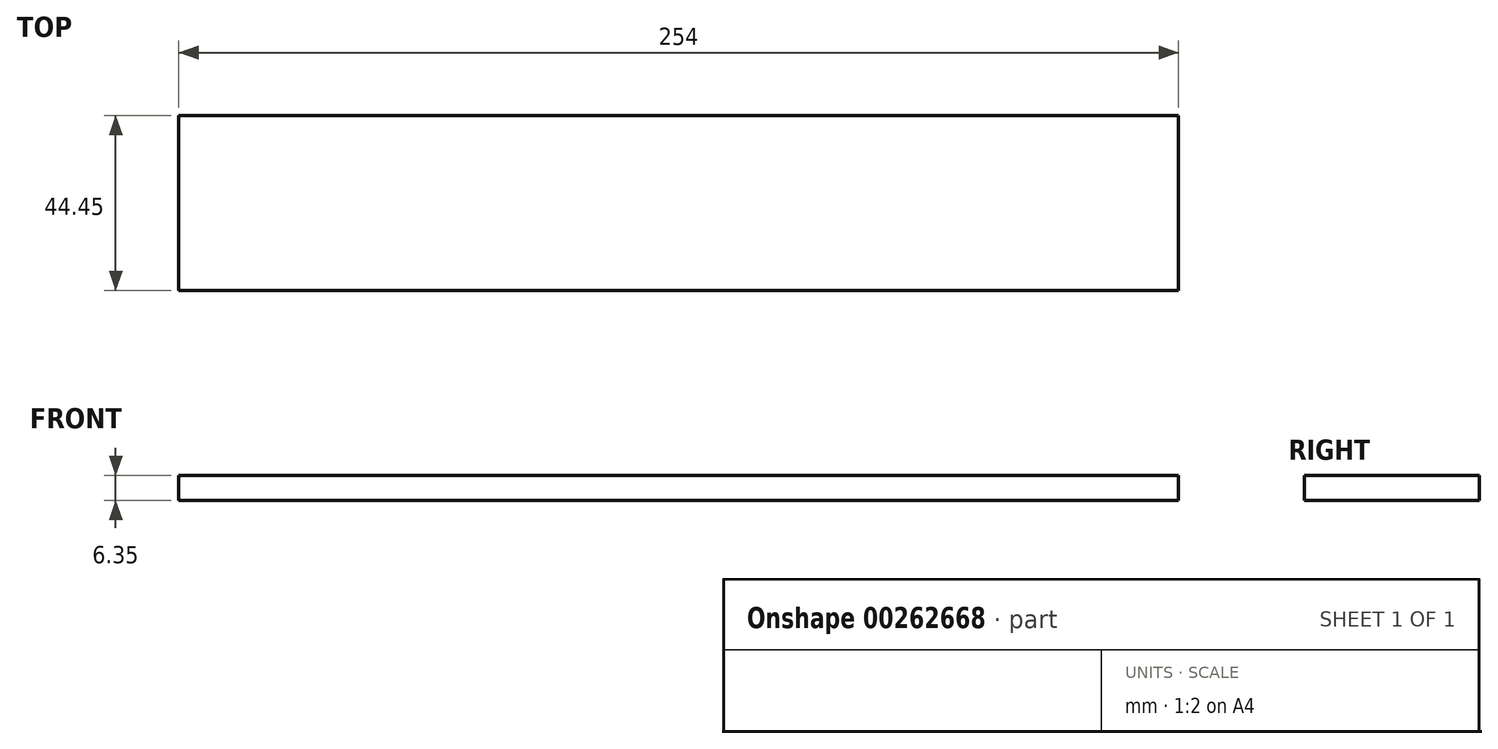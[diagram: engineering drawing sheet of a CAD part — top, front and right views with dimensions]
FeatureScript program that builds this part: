
annotation { "Feature Type Name" : "Feature", "Feature Type Description" : "" }
export const myFeature = defineFeature(function(context is Context, id is Id, definition is map)
    precondition{}
    {
        {
            var Q0;
            Q0=qCreatedBy(makeId("Top.planeOp"),FACE);
            var sketch = newSketch(context, id + "F0", { "sketchPlane" : qUnion([Q0])});
            skLineSegment(sketch, "E0.bottom", {"start": v(0, 0) * mm, "end": v(254, 0) * mm});
            skLineSegment(sketch, "E0.top", {"start": v(0, 44.45) * mm, "end": v(254, 44.45) * mm});
            skLineSegment(sketch, "E0.left", {"start": v(0, 0) * mm, "end": v(0, 44.45) * mm});
            skLineSegment(sketch, "E0.right", {"start": v(254, 0) * mm, "end": v(254, 44.45) * mm});
            skSolve(sketch);
        }
        {
            var Q0;
            Q0=makeQuery(id+"F0.imprint","IMPRINT",FACE,{"disambiguationData":[TD([[makeQuery(id+"F0.imprint","IMPRINT",EDGE,{"derivedFrom":sQuery(id+"F0.wireOp",EDGE,"E0.bottom")}),1.0]])]});
            extrude(context, id + "F1", {"entities" : qUnion([Q0]), "depth" : 6.35 * mm});
        }
    });
